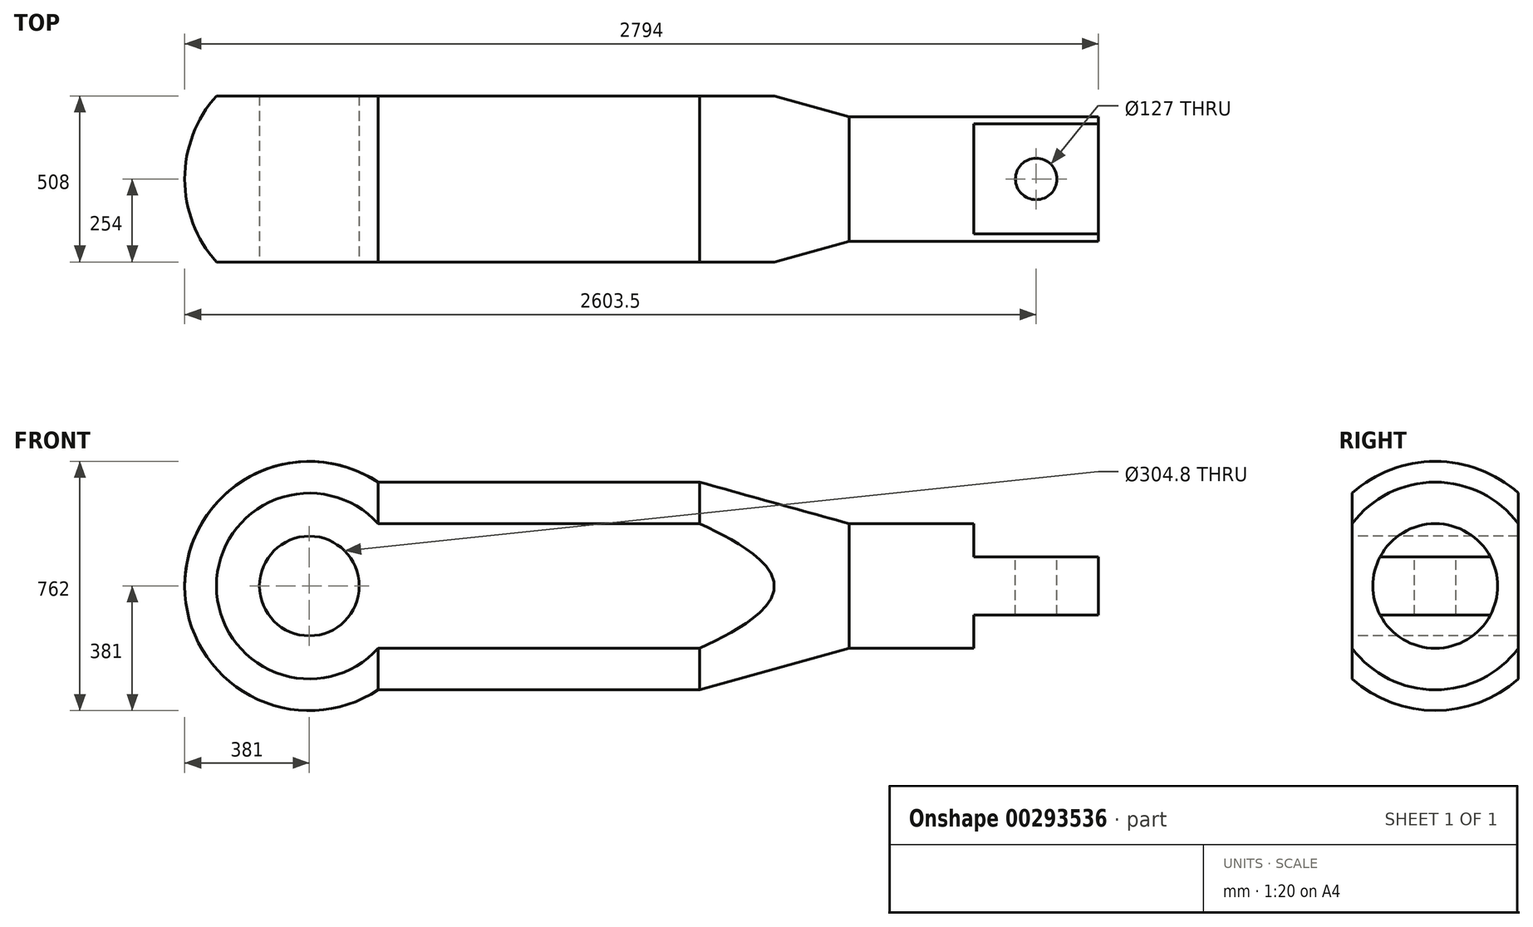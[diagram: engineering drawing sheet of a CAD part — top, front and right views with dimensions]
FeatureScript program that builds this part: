
annotation { "Feature Type Name" : "Feature", "Feature Type Description" : "" }
export const myFeature = defineFeature(function(context is Context, id is Id, definition is map)
    precondition{}
    {
        {
            var Q0;
            Q0=qCreatedBy(makeId("Front.planeOp"),FACE);
            var sketch = newSketch(context, id + "F0", { "sketchPlane" : qUnion([Q0])});
            skLineSegment(sketch, "E0", {"start": v(0, 0) * mm, "end": v(2814.61, 0) * mm, "construction": true});
            skArc(sketch, "E1", {"start": v(-381, 0) * mm, "mid": v(-180.17, 335.7) * mm, "end": v(210.6, 317.5) * mm});
            skLineSegment(sketch, "E2", {"start": v(210.6, 317.5) * mm, "end": v(1193.8, 317.5) * mm});
            skLineSegment(sketch, "E3", {"start": v(1193.8, 317.5) * mm, "end": v(1651, 190.5) * mm});
            skLineSegment(sketch, "E4", {"start": v(1651, 190.5) * mm, "end": v(2413, 190.5) * mm});
            skLineSegment(sketch, "E5", {"start": v(2413, 190.5) * mm, "end": v(2413, 0) * mm});
            skLineSegment(sketch, "E6", {"start": v(2413, 0) * mm, "end": v(-381, 0) * mm});
            skSolve(sketch);
        }
        {
            var Q0;
            Q0 = qSketchRegion(id + "F0", true);
            var Q1;
            Q1=sQuery(id+"F0.wireOp",EDGE,"E0");
            revolve(context, id + "F1", {"entities" : qUnion([Q0]), "axis" : qUnion([Q1]), "revolveType" : RevolveType.FULL});
        }
        {
            var Q0;
            Q0=qCreatedBy(makeId("Front.planeOp"),FACE);
            var sketch = newSketch(context, id + "F2", { "sketchPlane" : qUnion([Q0])});
            skLineSegment(sketch, "E7", {"start": v(2413, 88.9) * mm, "end": v(2032, 88.9) * mm});
            skLineSegment(sketch, "E8", {"start": v(2032, 88.9) * mm, "end": v(2032, 190.5) * mm});
            skLineSegment(sketch, "E9", {"start": v(2413, 190.5) * mm, "end": v(2413, 88.9) * mm});
            skLineSegment(sketch, "E10", {"start": v(2032, 190.5) * mm, "end": v(2413, 190.5) * mm});
            skLineSegment(sketch, "E11", {"start": v(1796.85, 0) * mm, "end": v(2495.61, 0) * mm, "construction": true});
            skLineSegment(sketch, "E12.MirrorCS", {"start": v(2032, -190.5) * mm, "end": v(2413, -190.5) * mm});
            skLineSegment(sketch, "E13.MirrorCS", {"start": v(2413, -88.9) * mm, "end": v(2032, -88.9) * mm});
            skLineSegment(sketch, "E14.MirrorCS", {"start": v(2413, -190.5) * mm, "end": v(2413, -88.9) * mm});
            skLineSegment(sketch, "E15.MirrorCS", {"start": v(2032, -88.9) * mm, "end": v(2032, -190.5) * mm});
            skSolve(sketch);
        }
        {
            var Q0;
            Q0 = qSketchRegion(id + "F2", true);
            extrude(context, id + "F3", {"entities" : qUnion([Q0]), "operationType" : NewBodyOperationType.REMOVE, "endBound" : BoundingType.THROUGH_ALL, "oppositeDirection" : true, "depth" : 25.4 * mm, "hasSecondDirection" : true, "secondDirectionBound" : SecondDirectionBoundingType.THROUGH_ALL, "secondDirectionOppositeDirection" : false, "secondDirectionDepth" : 25.4 * mm});
        }
        {
            var Q0;
            Q0=makeQuery(id+"F1.opRevolve","SWEPT_FACE",FACE,{"disambiguationData":[OSD([sQuery(id+"F0.wireOp",EDGE,"E5")])]});
            var sketch = newSketch(context, id + "F4", { "sketchPlane" : qUnion([Q0])});
            skLineSegment(sketch, "E16", {"start": v(-254, 283.98) * mm, "end": v(-254, -283.98) * mm});
            skArc(sketch, "E17", {"start": v(-254, 283.98) * mm, "mid": v(-381, 0) * mm, "end": v(-254, -283.98) * mm});
            skLineSegment(sketch, "E18", {"start": v(254, 283.98) * mm, "end": v(254, -283.98) * mm});
            skLineSegment(sketch, "E19", {"start": v(0, 528.84) * mm, "end": v(0, 0) * mm, "construction": true});
            skArc(sketch, "E20.trimOffspring", {"start": v(254, -283.98) * mm, "mid": v(381, 0) * mm, "end": v(254, 283.98) * mm});
            skSolve(sketch);
        }
        {
            var Q0;
            Q0 = qSketchRegion(id + "F4", true);
            extrude(context, id + "F5", {"entities" : qUnion([Q0]), "operationType" : NewBodyOperationType.REMOVE, "endBound" : BoundingType.THROUGH_ALL, "oppositeDirection" : true, "depth" : 25.4 * mm});
        }
        {
            var Q0;
            Q0=makeQuery(id+"F5.boolean.opBoolean","COPY",FACE,{"derivedFrom":makeQuery(id+"F5.opExtrude","SWEPT_FACE",FACE,{"disambiguationData":[OSD([sQuery(id+"F4.wireOp",EDGE,"E16")])]})});
            var sketch = newSketch(context, id + "F6", { "sketchPlane" : qUnion([Q0])});
            skCircle(sketch, "E21", {"center": v(0, 0) * mm, "radius": 152.4 * mm});
            skSolve(sketch);
        }
        {
            var Q0;
            Q0 = qSketchRegion(id + "F6", true);
            extrude(context, id + "F7", {"entities" : qUnion([Q0]), "operationType" : NewBodyOperationType.REMOVE, "endBound" : BoundingType.THROUGH_ALL, "oppositeDirection" : true, "depth" : 25.4 * mm});
        }
        {
            var Q0;
            Q0=makeQuery(id+"F3.boolean.opBoolean","COPY",FACE,{"derivedFrom":makeQuery(id+"F3.opExtrude","SWEPT_FACE",FACE,{"disambiguationData":[OSD([sQuery(id+"F2.wireOp",EDGE,"E7")])]})});
            var sketch = newSketch(context, id + "F8", { "sketchPlane" : qUnion([Q0])});
            skCircle(sketch, "E22", {"center": v(2222.5, 0) * mm, "radius": 63.5 * mm});
            skPoint(sketch, "E22.centerSnap0", {"position": v(2222.5, 168.48) * mm});
            skSolve(sketch);
        }
        {
            var Q0;
            Q0 = qSketchRegion(id + "F8", true);
            extrude(context, id + "F9", {"entities" : qUnion([Q0]), "operationType" : NewBodyOperationType.REMOVE, "endBound" : BoundingType.THROUGH_ALL, "oppositeDirection" : true, "depth" : 25.4 * mm});
        }
    });
